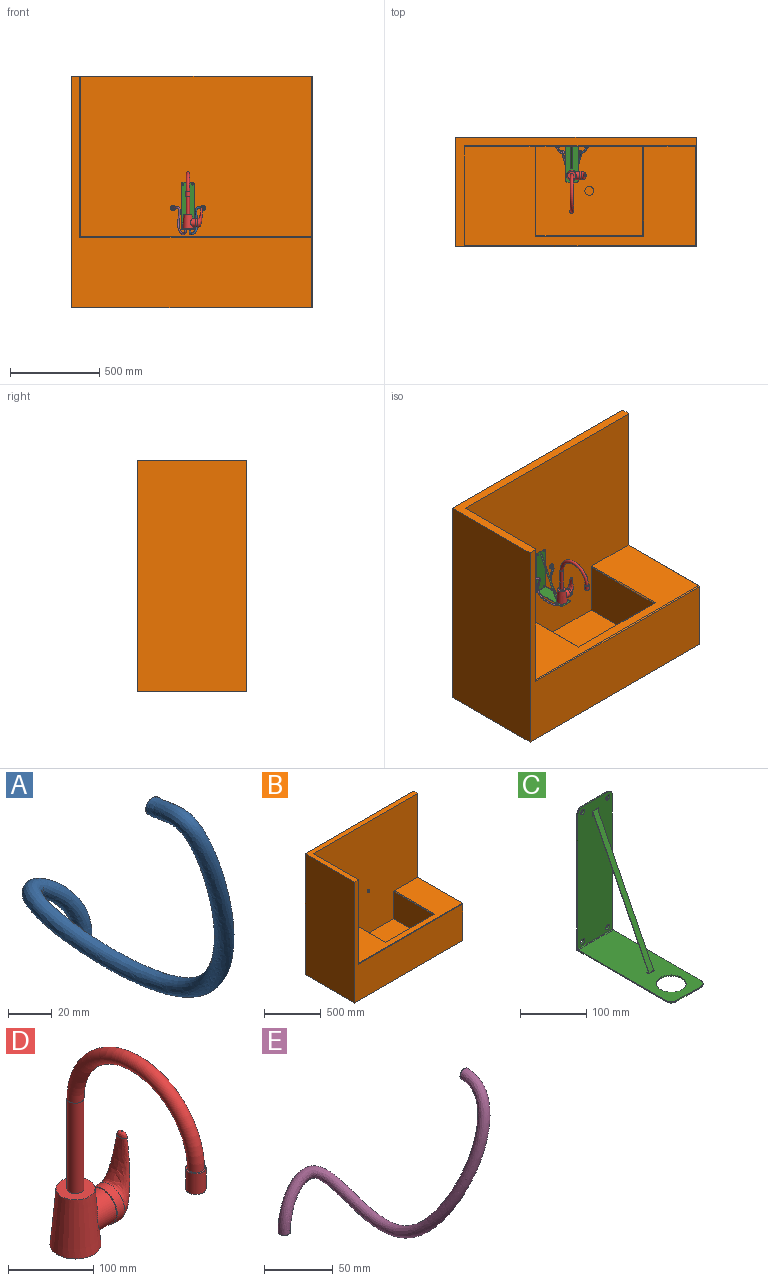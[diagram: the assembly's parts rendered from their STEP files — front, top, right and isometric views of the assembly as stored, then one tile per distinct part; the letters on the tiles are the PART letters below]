
ASSEMBLY  parts=5 mates=4
PART A: 3 faces, bbox 86.4x165.9x174.2 mm
  f0: plane 9x9mm, normal (0,0,-1), area 63.6mm2, adj f2
  f1: plane 9x9mm, normal (0,1,0), area 63.6mm2, adj f2
  f2: bspline ~174.23x165.9mm, area 9408.9mm2, adj f0,f1
PART B: 34 faces, bbox 1350x615x1300 mm
  f0: plane 1345x1300mm, normal (0,-1,0), area 572000mm2, adj f6,f10,f11,f25,f26,f27
  f1: plane 1300x610mm, normal (1,0,0), area 281675mm2, adj f6,f9,f11,f26,f29,f30
  f2: plane 500x295mm, normal (-1,0,0), area 147500mm2, adj f3,f8,f12,f31
  f3: plane 600x295mm, normal (0,1,0), area 177000mm2, adj f2,f4,f12,f32
  f4: plane 500x295mm, normal (1,0,0), area 147500mm2, adj f3,f8,f12,f33
  f5: plane 1295x560mm, normal (0,0,1), area 417150mm2, adj f7,f8,f27,f29,f31,f32,f33
  f6: plane 1350x615mm, normal (0,0,-1), area 830237.5mm2, adj f0,f1,f9,f10,f26
  f7: plane 900x560mm, normal (1,0,0), area 504000mm2, adj f5,f8,f11,f25
  f8: plane 1295x1200mm, normal (0,-1,0), area 1344199.4mm2, adj f2,f4,f5,f7,f11,f12,f21,f22
  f9: plane 1350x1300mm, normal (0,1,0), area 1755000mm2, adj f1,f6,f10,f11
  f10: plane 1300x615mm, normal (-1,0,0), area 799500mm2, adj f0,f6,f9,f11
  f11: plane 1350x615mm, normal (0,0,1), area 95725mm2, adj f0,f1,f7,f8,f9,f10,f25,f30
  f12: plane 600x500mm, normal (0,0,1), area 298036.5mm2, adj f2,f3,f4,f8,f23
  f13: plane 25.05x25.05mm, normal (0,-1,0), area 207.8mm2, adj f14,f15
  f14: cylinder r=12.53mm len=25.05mm, axis (0,-1,0), area 393.5mm2, adj f13,f22
  f15: cylinder r=9.53mm len=19.05mm, axis (0,-1,0), area 418.9mm2, adj f13,f16
  f16: plane 19.05x19.05mm, normal (0,-1,0), area 285mm2, adj f15
  f17: plane 25.05x25.05mm, normal (0,-1,0), area 207.8mm2, adj f18,f19
  f18: cylinder r=12.53mm len=25.05mm, axis (0,-1,0), area 393.5mm2, adj f17,f21
  f19: cylinder r=9.53mm len=19.05mm, axis (0,-1,0), area 418.9mm2, adj f17,f20
  f20: plane 19.05x19.05mm, normal (0,-1,0), area 285mm2, adj f19
  f21: torus R=14.53mm, axis (0,1,0), area 261.6mm2, adj f8,f18
  f22: torus R=14.53mm, axis (0,1,0), area 261.6mm2, adj f8,f14
  f23: cylinder r=25mm len=50mm, axis (0,0,1), area 1570.8mm2, adj f12,f24
  f24: plane 50x50mm, normal (0,0,1), area 1963.5mm2, adj f23
  f25: plane 905x5mm, normal (0.71,-0.71,0), area 6381.6mm2, adj f0,f7,f11,f27
  f26: plane 395x5mm, normal (0.71,-0.71,0), area 2793.1mm2, adj f0,f1,f6,f28
  f27: plane 1300x5mm, normal (0,-0.71,0.71), area 9174.7mm2, adj f0,f5,f25,f28
  f28: plane 5x5mm, normal (0.58,-0.58,0.58), area 21.7mm2, adj f26,f27,f29
  f29: plane 565x5mm, normal (0.71,0,0.71), area 3977.5mm2, adj f1,f5,f28,f30
  f30: plane 905x5mm, normal (0.71,-0.71,0), area 6381.6mm2, adj f1,f8,f11,f29
  f31: plane 505x5mm, normal (-0.71,0,0.71), area 3553.2mm2, adj f2,f5,f8,f32
  f32: plane 610x5mm, normal (0,0.71,0.71), area 4278mm2, adj f3,f5,f31,f33
  f33: plane 505x5mm, normal (0.71,0,0.71), area 3553.2mm2, adj f4,f5,f8,f32
PART C: 30 faces, bbox 81.8x202.4x262.4 mm
  f0: plane 258.5x74mm, normal (0,-1,0), area 18717.6mm2, adj f3,f4,f5,f14,f15,f17,f18,f19
  f1: plane 198.5x74mm, normal (0,0,1), area 12997.5mm2, adj f3,f4,f7,f12,f13,f16,f21,f22
  f2: plane 262x74mm, normal (0,1,0), area 19267.8mm2, adj f3,f4,f5,f6,f14,f15,f17,f18
  f3: plane 252.38x192.38mm, normal (-1,0,0), area 884.8mm2, adj f0,f1,f2,f6,f12,f14,f29
  f4: plane 252.38x192.38mm, normal (1,0,0), area 884.8mm2, adj f0,f1,f2,f6,f13,f15,f29
  f5: plane 54x2mm, normal (0,0,1), area 108mm2, adj f0,f2,f14,f15
  f6: plane 202x74mm, normal (0,0,-1), area 13314.6mm2, adj f2,f3,f4,f7,f12,f13,f16
  f7: plane 54x2mm, normal (0,-1,0), area 108mm2, adj f1,f6,f12,f13
  f8: plane 240.35x120.39mm, normal (0,-0.89,0.45), area 2685.4mm2, adj f9,f10,f21,f22,f23,f25,f26,f28
  f9: plane 236.78x118.5mm, normal (1,0,0), area 264.4mm2, adj f8,f11,f23,f24,f27,f28
  f10: plane 236.78x118.51mm, normal (-1,0,0), area 264.4mm2, adj f8,f11,f22,f24,f25,f27
  f11: plane 231.03x115.55mm, normal (0,0.89,-0.45), area 2583.1mm2, adj f9,f10,f24,f27
  f12: cylinder r=10mm len=10mm, axis (0,0,1), area 31.4mm2, adj f1,f3,f6,f7
  f13: cylinder r=10mm len=10mm, axis (0,0,-1), area 31.4mm2, adj f1,f4,f6,f7
  f14: cylinder r=10mm len=10mm, axis (0,1,0), area 31.4mm2, adj f0,f2,f3,f5
  f15: cylinder r=10mm len=10mm, axis (0,-1,0), area 31.4mm2, adj f0,f2,f4,f5
  f16: cylinder r=22.5mm len=45mm, axis (0,0,1), area 282.7mm2, adj f1,f6
  f17: cone r=2.2mm half-angle=45deg, axis (0,-1,0), area 61.8mm2, adj f0,f2
  f18: cone r=2.2mm half-angle=45deg, axis (0,-1,0), area 61.8mm2, adj f0,f2
  f19: cone r=2.2mm half-angle=45deg, axis (0,-1,0), area 61.8mm2, adj f0,f2
  f20: cone r=2.2mm half-angle=45deg, axis (0,-1,0), area 61.8mm2, adj f0,f2
  f21: bspline ~13.43x1.34mm, area 19mm2, adj f1,f8,f22,f23
  f22: bspline ~4.92x1.5mm, area 5.9mm2, adj f1,f8,f10,f21,f24
  f23: bspline ~4.77x1.5mm, area 5.9mm2, adj f1,f8,f9,f21,f24
  f24: bspline ~13.43x2.43mm, area 30.3mm2, adj f1,f9,f10,f11,f22,f23
  f25: bspline ~9.54x1.5mm, area 13.8mm2, adj f0,f8,f10,f26,f27
  f26: bspline ~13.43x0.67mm, area 8.7mm2, adj f0,f8,f25,f28
  f27: bspline ~13.43x6.35mm, area 44.7mm2, adj f0,f9,f10,f11,f25,f28
  f28: bspline ~9.84x1.5mm, area 13.8mm2, adj f0,f8,f9,f26,f27
  f29: bspline ~81.4x1.5mm, area 162.5mm2, adj f0,f1,f3,f4
PART D: 22 faces, bbox 111.5x249.1x329.1 mm
  f0: cone r=30mm half-angle=5deg, axis (0,0,-1), area 11480mm2, adj f1,f2,f3
  f1: plane 46x46mm, normal (0,0,1), area 1347.9mm2, adj f0,f10
  f2: plane 60x60mm, normal (0,0,-1), area 2726.9mm2, adj f0,f18,f20
  f3: cylinder r=23.01mm len=46.02mm, axis (-1,0,0), area 3440mm2, adj f0,f5
  f4: cylinder r=24.51mm len=49.02mm, axis (-1,0,0), area 1847.9mm2, adj f5,f6
  f5: plane 49.02x49.02mm, normal (-1,0,0), area 223.9mm2, adj f3,f4
  f6: bspline ~108.9x49.02mm, area 6987.1mm2, adj f4,f8
  f7: plane 0.33x0.33mm, normal (0,0,1), area 0.1mm2, adj f8
  f8: bspline ~15x8.37mm, area 237.9mm2, adj f6,f7
  f9: plane 24x24mm, normal (0,0,-1), area 275.7mm2, adj f14,f16
  f10: cylinder r=10mm len=130mm, axis (0,0,1), area 8168.1mm2, adj f1,f11
  f11: torus R=100mm, axis (1,0,0), area 19739.2mm2, adj f10,f15
  f12: cylinder r=7.5mm len=130mm, axis (0,0,1), area 6126.1mm2, adj f13,f17
  f13: torus R=100mm, axis (1,0,0), area 14804.4mm2, adj f12,f14
  f14: cylinder r=7.5mm len=30mm, axis (0,0,-1), area 1413.7mm2, adj f9,f13
  f15: plane 24x24mm, normal (0,0,1), area 138.2mm2, adj f11,f16
  f16: cylinder r=12mm len=30mm, axis (0,0,-1), area 2261.9mm2, adj f9,f15
  f17: plane 15x15mm, normal (0,0,1), area 176.7mm2, adj f12
  f18: cylinder r=4mm len=25mm, axis (0,0,-1), area 628.3mm2, adj f2,f19
  f19: plane 8x8mm, normal (0,0,-1), area 50.3mm2, adj f18
  f20: cylinder r=4mm len=25mm, axis (0,0,-1), area 628.3mm2, adj f2,f21
  f21: plane 8x8mm, normal (0,0,-1), area 50.3mm2, adj f20
PART E: 3 faces, bbox 83x166.6x170.8 mm
  f0: plane 9x9mm, normal (0,0,-1), area 63.6mm2, adj f2
  f1: plane 9x9mm, normal (0,1,0), area 63.6mm2, adj f2
  f2: bspline ~170.83x166.65mm, area 9142.3mm2, adj f0,f1
PLACE A rot(axis=(1,0,0),90deg) t=(-180,0,560)mm
PLACE B at identity fixed
PLACE C t=(-98.6,-165,443.4)mm
PLACE D t=(-98.6,-165,443.4)mm
PLACE E rot(axis=(1,0,0),90deg) t=(-180,0,560)mm
MATE planar C.f15 <-> B.f8  axis (0,1,0) through (-71.6,0,693.4)mm
MATE fastened B.f14 <-> E.f0  axis (0,-1,0) through (-180,0,560)mm
MATE fastened D.f0 <-> C.f16  axis (0,0,1) through (-98.6,-165,443.4)mm
MATE fastened A.f0 <-> B.f18  axis (0,-1,0) through (-15,0,560)mm
